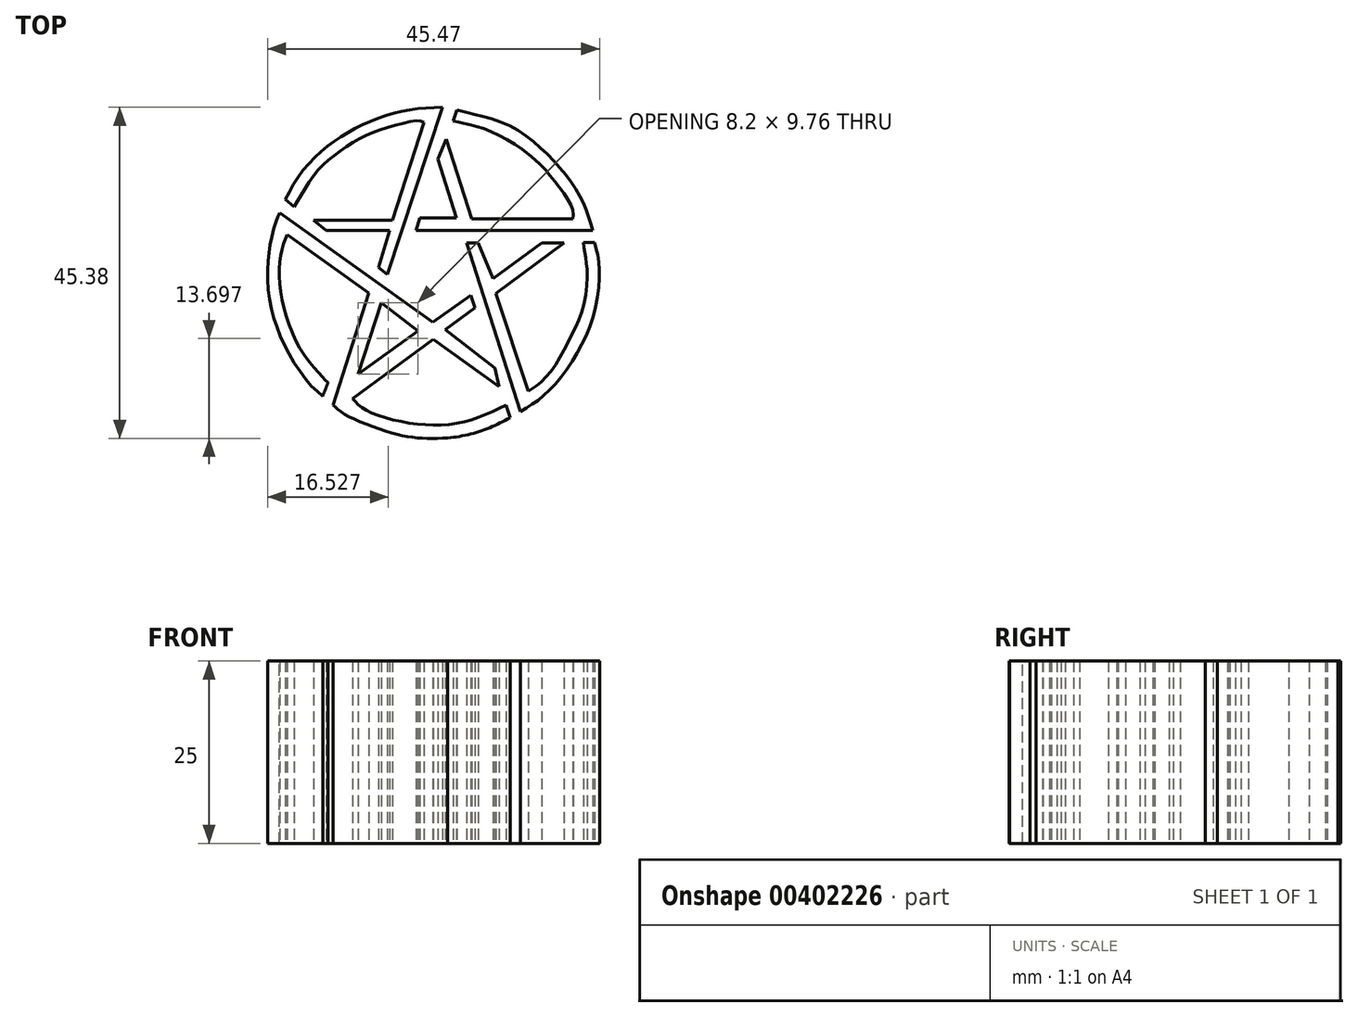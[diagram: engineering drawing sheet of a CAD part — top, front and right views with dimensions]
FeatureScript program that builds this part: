
annotation { "Feature Type Name" : "Feature", "Feature Type Description" : "" }
export const myFeature = defineFeature(function(context is Context, id is Id, definition is map)
    precondition{}
    {
        {
            var Q0;
            Q0=qCreatedBy(makeId("Top.planeOp"),FACE);
            var sketch = newSketch(context, id + "F0", { "sketchPlane" : qUnion([Q0])});
            skLineSegment(sketch, "E0", {"start": v(34.04, 53.7) * mm, "end": v(44.81, 53.7) * mm});
            skLineSegment(sketch, "E1", {"start": v(44.81, 53.7) * mm, "end": v(49.17, 67.07) * mm});
            skLineSegment(sketch, "E2", {"start": v(34.04, 53.7) * mm, "end": v(35.73, 52.33) * mm});
            skLineSegment(sketch, "E3", {"start": v(35.73, 52.33) * mm, "end": v(44.46, 52.33) * mm});
            skLineSegment(sketch, "E4", {"start": v(44.46, 52.33) * mm, "end": v(42.94, 47.22) * mm});
            skLineSegment(sketch, "E5", {"start": v(42.94, 47.22) * mm, "end": v(44.11, 46.28) * mm});
            skLineSegment(sketch, "E6", {"start": v(44.11, 46.28) * mm, "end": v(51.7, 69.18) * mm});
            skFitSpline(sketch, "E7", {"points": [v(51.7, 69.18) * mm, v(48, 68.94) * mm, v(44.54, 68.25) * mm, v(40.97, 66.87) * mm, v(37.72, 65.1) * mm, v(34.85, 62.93) * mm, v(32.08, 59.86) * mm, v(30.19, 56.57) * mm], "startDerivative": vector(-26.32, -1.03) * mm, "endDerivative": vector(-11.91, -23.24) * mm});
            skFitSpline(sketch, "E8", {"points": [v(30.19, 56.57) * mm, v(31.36, 55.54) * mm], "startDerivative": vector(1.17, -1.02) * mm, "endDerivative": vector(1.17, -1.02) * mm});
            skFitSpline(sketch, "E9", {"points": [v(31.36, 55.54) * mm, v(32.78, 57.87) * mm, v(34.73, 60.66) * mm, v(36.8, 62.53) * mm, v(39.62, 64.45) * mm, v(42.3, 65.8) * mm, v(45.8, 66.87) * mm, v(48.25, 67.35) * mm, v(49.17, 67.07) * mm], "startDerivative": vector(10.85, 17.86) * mm, "endDerivative": vector(11, -5.12) * mm});
            skLineSegment(sketch, "E10", {"start": v(69.52, 53.9) * mm, "end": v(55.7, 53.9) * mm});
            skLineSegment(sketch, "E11", {"start": v(55.7, 53.9) * mm, "end": v(52.17, 64.82) * mm});
            skLineSegment(sketch, "E12", {"start": v(52.17, 64.82) * mm, "end": v(51.04, 62.06) * mm});
            skLineSegment(sketch, "E13", {"start": v(51.04, 62.06) * mm, "end": v(53.6, 54) * mm});
            skLineSegment(sketch, "E14", {"start": v(53.6, 54) * mm, "end": v(48.57, 54) * mm});
            skLineSegment(sketch, "E15", {"start": v(48.57, 54) * mm, "end": v(48.06, 52.28) * mm});
            skLineSegment(sketch, "E16", {"start": v(48.06, 52.28) * mm, "end": v(72.28, 52.28) * mm});
            skFitSpline(sketch, "E17", {"points": [v(72.28, 52.28) * mm, v(71.22, 55.45) * mm, v(69.13, 59.2) * mm, v(65.58, 63.18) * mm, v(61, 66.58) * mm, v(55.94, 68.25) * mm, v(53.67, 68.8) * mm], "startDerivative": vector(-6.17, 21.35) * mm, "endDerivative": vector(-17.8, 3.56) * mm});
            skFitSpline(sketch, "E18", {"points": [v(53.67, 68.8) * mm, v(53.14, 67.3) * mm], "startDerivative": vector(-0.53, -1.48) * mm, "endDerivative": vector(-0.53, -1.48) * mm});
            skFitSpline(sketch, "E19", {"points": [v(53.14, 67.3) * mm, v(55.25, 66.85) * mm, v(58.75, 65.68) * mm, v(63.16, 63) * mm, v(65.95, 60.4) * mm, v(68.2, 57.5) * mm, v(69.52, 55.1) * mm, v(69.52, 53.9) * mm], "startDerivative": vector(16.75, -3.37) * mm, "endDerivative": vector(-1.88, -12.56) * mm});
            skLineSegment(sketch, "E20", {"start": v(63.45, 30.3) * mm, "end": v(59, 43.68) * mm});
            skLineSegment(sketch, "E21", {"start": v(59, 43.68) * mm, "end": v(68.32, 50.57) * mm});
            skLineSegment(sketch, "E22", {"start": v(68.32, 50.57) * mm, "end": v(65.26, 50.57) * mm});
            skLineSegment(sketch, "E23", {"start": v(65.26, 50.57) * mm, "end": v(58.59, 45.67) * mm});
            skLineSegment(sketch, "E24", {"start": v(58.59, 45.67) * mm, "end": v(56.6, 50.57) * mm});
            skLineSegment(sketch, "E25", {"start": v(56.6, 50.57) * mm, "end": v(54.97, 50.57) * mm});
            skLineSegment(sketch, "E26", {"start": v(54.97, 50.57) * mm, "end": v(62.37, 27.48) * mm});
            skFitSpline(sketch, "E27", {"points": [v(62.37, 27.48) * mm, v(65.44, 29.58) * mm, v(69.22, 34.03) * mm, v(72.32, 40.57) * mm, v(73.16, 47.2) * mm, v(72.49, 50.64) * mm], "startDerivative": vector(18.2, 10.77) * mm, "endDerivative": vector(-5.41, 19.2) * mm});
            skFitSpline(sketch, "E28", {"points": [v(72.49, 50.64) * mm, v(70.97, 50.64) * mm], "startDerivative": vector(-1.52, 0) * mm, "endDerivative": vector(-1.52, 0) * mm});
            skFitSpline(sketch, "E29", {"points": [v(70.97, 50.64) * mm, v(71.23, 48.9) * mm, v(71.48, 46.77) * mm, v(70.97, 41.87) * mm, v(69.3, 37.88) * mm, v(67.04, 33.71) * mm, v(64.86, 31.24) * mm, v(63.45, 30.3) * mm], "startDerivative": vector(2.34, -16.4) * mm, "endDerivative": vector(-12.91, -7.73) * mm});
            skLineSegment(sketch, "E30", {"start": v(40.14, 32.62) * mm, "end": v(48.35, 38.51) * mm});
            skLineSegment(sketch, "E31", {"start": v(48.35, 38.51) * mm, "end": v(43.3, 42.38) * mm});
            skLineSegment(sketch, "E32", {"start": v(43.3, 42.38) * mm, "end": v(40.14, 32.62) * mm});
            skLineSegment(sketch, "E33", {"start": v(29.4, 54.73) * mm, "end": v(50.33, 39.74) * mm});
            skLineSegment(sketch, "E34", {"start": v(50.33, 39.74) * mm, "end": v(55.55, 43.44) * mm});
            skLineSegment(sketch, "E35", {"start": v(55.55, 43.44) * mm, "end": v(56.12, 41.68) * mm});
            skLineSegment(sketch, "E36", {"start": v(56.12, 41.68) * mm, "end": v(52.06, 38.71) * mm});
            skLineSegment(sketch, "E37", {"start": v(52.06, 38.71) * mm, "end": v(58.87, 33.42) * mm});
            skLineSegment(sketch, "E38", {"start": v(58.87, 33.42) * mm, "end": v(59.43, 30.91) * mm});
            skLineSegment(sketch, "E39", {"start": v(59.43, 30.91) * mm, "end": v(50.44, 37.37) * mm});
            skLineSegment(sketch, "E40", {"start": v(50.44, 37.37) * mm, "end": v(39.34, 29.27) * mm});
            skFitSpline(sketch, "E41", {"points": [v(39.34, 29.27) * mm, v(41.09, 27.76) * mm, v(47.13, 25.91) * mm, v(54.3, 26) * mm, v(60.39, 28.35) * mm], "startDerivative": vector(8.43, -9.43) * mm, "endDerivative": vector(21.43, 10.22) * mm});
            skFitSpline(sketch, "E42", {"points": [v(60.39, 28.35) * mm, v(60.94, 26.63) * mm], "startDerivative": vector(0.55, -1.72) * mm, "endDerivative": vector(0.55, -1.72) * mm});
            skFitSpline(sketch, "E43", {"points": [v(60.94, 26.63) * mm, v(56.95, 24.82) * mm, v(52.37, 23.86) * mm], "startDerivative": vector(-7.88, -4.22) * mm, "endDerivative": vector(-9.4, -0.92) * mm});
            skFitSpline(sketch, "E44", {"points": [v(52.37, 23.86) * mm, v(48.47, 23.86) * mm, v(44.15, 24.74) * mm, v(38.4, 27.05) * mm, v(36.68, 28.39) * mm], "startDerivative": vector(-16.03, -0.6) * mm, "endDerivative": vector(-7.37, 7.1) * mm});
            skLineSegment(sketch, "E45", {"start": v(36.68, 28.39) * mm, "end": v(41.62, 43.71) * mm});
            skLineSegment(sketch, "E46", {"start": v(41.62, 43.71) * mm, "end": v(30.44, 51.73) * mm});
            skFitSpline(sketch, "E47", {"points": [v(30.44, 51.73) * mm, v(29.72, 49.75) * mm, v(29.3, 46.18) * mm, v(30.08, 41.23) * mm, v(32.36, 35.83) * mm, v(35.04, 32.45) * mm, v(36.01, 31.47) * mm], "startDerivative": vector(-5.94, -14.25) * mm, "endDerivative": vector(8.25, -7.93) * mm});
            skFitSpline(sketch, "E48", {"points": [v(36.01, 31.47) * mm, v(35.28, 29.58) * mm], "startDerivative": vector(-0.6, -1.66) * mm, "endDerivative": vector(-0.6, -1.66) * mm});
            skFitSpline(sketch, "E49", {"points": [v(35.28, 29.58) * mm, v(33.2, 31.6) * mm, v(30.56, 35.6) * mm, v(28.78, 39.69) * mm, v(27.83, 43.93) * mm, v(27.8, 48.17) * mm, v(28.27, 51.28) * mm, v(29.01, 53.86) * mm, v(29.4, 54.73) * mm], "startDerivative": vector(-17.5, 15.06) * mm, "endDerivative": vector(5.51, 11.03) * mm});
            skFitSpline(sketch, "E50", {"points": [v(48.98, 97.92) * mm, v(51.03, 96.75) * mm, v(53.35, 94.5) * mm, v(55.25, 91.65) * mm, v(55.6, 89.02) * mm, v(55.25, 86) * mm, v(54.5, 83.74) * mm, v(53.6, 81.36) * mm, v(53.16, 79.9) * mm, v(53.34, 77.77) * mm, v(53.96, 76.35) * mm, v(54.68, 75.1) * mm, v(55.25, 74.9) * mm, v(55.94, 75.48) * mm], "startDerivative": vector(24.94, -12.18) * mm, "endDerivative": vector(6.73, 19.15) * mm});
            skFitSpline(sketch, "E51", {"points": [v(55.94, 75.48) * mm, v(56.87, 76.84) * mm, v(58.58, 78.29) * mm, v(60.14, 79.6) * mm, v(61.46, 80.8) * mm, v(62.6, 82.4) * mm, v(63.4, 84.14) * mm, v(63.64, 85.48) * mm, v(63.7, 86.9) * mm, v(63.65, 87.79) * mm, v(63.57, 88.08) * mm], "startDerivative": vector(7.59, 13.14) * mm, "endDerivative": vector(-1.96, 5.62) * mm});
            skFitSpline(sketch, "E52", {"points": [v(63.57, 88.08) * mm, v(64.2, 87.56) * mm, v(64.8, 86.8) * mm, v(65.33, 85.8) * mm, v(65.89, 84.56) * mm, v(66.17, 83.5) * mm, v(66.4, 81.93) * mm, v(65.96, 80.43) * mm, v(65.24, 78.88) * mm, v(63.83, 76.9) * mm, v(62.85, 75.26) * mm, v(62.4, 74.38) * mm, v(62.3, 73.64) * mm, v(62.37, 72.64) * mm, v(62.68, 72.24) * mm], "startDerivative": vector(10.96, -8.33) * mm, "endDerivative": vector(8.06, -6.97) * mm});
            skFitSpline(sketch, "E53", {"points": [v(62.68, 72.24) * mm, v(63.23, 72.24) * mm, v(64.21, 73.18) * mm, v(65.93, 74.42) * mm, v(67.75, 75.1) * mm, v(69.88, 75.89) * mm, v(71.74, 76.8) * mm, v(73.4, 78) * mm, v(74.88, 79.81) * mm, v(75.51, 81.51) * mm, v(75.9, 82.72) * mm], "startDerivative": vector(9.62, -2.12) * mm, "endDerivative": vector(4.66, 13.44) * mm});
            skFitSpline(sketch, "E54", {"points": [v(75.9, 82.72) * mm, v(76.41, 81.51) * mm, v(76.78, 79.84) * mm, v(76.96, 78.08) * mm, v(76.85, 76.35) * mm, v(75.55, 74.85) * mm, v(73.9, 73.15) * mm, v(72.27, 71.97) * mm, v(70.64, 70.7) * mm, v(70.2, 70.03) * mm, v(70.3, 69.57) * mm, v(71.38, 69.73) * mm, v(72.94, 69.96) * mm, v(75.39, 69.98) * mm, v(77.82, 70) * mm, v(79.84, 70.56) * mm, v(82.24, 71.53) * mm, v(83.84, 73.42) * mm, v(84.53, 74.25) * mm], "startDerivative": vector(11.08, -23.6) * mm, "endDerivative": vector(14.5, 16.03) * mm});
            skFitSpline(sketch, "E55", {"points": [v(84.53, 74.25) * mm, v(85.03, 73.14) * mm, v(84.53, 70.54) * mm, v(83.39, 68.15) * mm, v(81.17, 66.47) * mm, v(78.4, 65.5) * mm, v(75.9, 64.75) * mm, v(74.54, 63.95) * mm, v(73.4, 62.36) * mm, v(72.65, 60.93) * mm, v(72.65, 60.13) * mm, v(72.98, 59.92) * mm, v(73.36, 59.84) * mm, v(74.03, 60.13) * mm, v(75.37, 61.35) * mm, v(77.8, 62.1) * mm, v(80.54, 62.31) * mm, v(82.97, 61.85) * mm, v(85.61, 61.1) * mm, v(87.92, 60.51) * mm, v(90.1, 60.22) * mm, v(92.5, 60.17) * mm, v(94.13, 60.6) * mm, v(95.52, 61.01) * mm, v(96.23, 61.56) * mm, v(97.03, 62.19) * mm, v(98.25, 63.07) * mm, v(98.7, 63.45) * mm, v(99.08, 63.49) * mm, v(99.3, 63.43) * mm, v(99.38, 62.94) * mm, v(99.17, 62.31) * mm, v(98.29, 60.68) * mm], "startDerivative": vector(23.51, -34.02) * mm, "endDerivative": vector(-27.36, -51.65) * mm});
            skFitSpline(sketch, "E56", {"points": [v(98.29, 60.68) * mm, v(97.69, 59.5) * mm, v(96.69, 57.53) * mm, v(95.5, 56.24) * mm, v(94.12, 55.33) * mm, v(91.9, 54.6) * mm, v(89.04, 54.37) * mm, v(86.47, 54.35) * mm, v(82.3, 53.66) * mm, v(80.4, 52.32) * mm, v(79.56, 51.26) * mm, v(79.7, 50.84) * mm, v(80.05, 50.77) * mm, v(81.32, 50.42) * mm, v(83.16, 49.64) * mm, v(85.41, 48.23) * mm, v(88.3, 46.82) * mm, v(90.57, 46.46) * mm, v(92.83, 46.82) * mm, v(95.01, 47.6) * mm], "startDerivative": vector(-13.33, -24.83) * mm, "endDerivative": vector(37.72, 14.89) * mm});
            skFitSpline(sketch, "E57", {"points": [v(95.01, 47.6) * mm, v(94.35, 45.8) * mm, v(92.25, 43.88) * mm, v(90.28, 42.53) * mm, v(88.16, 42.45) * mm, v(85.52, 42.93) * mm, v(83.3, 43.55) * mm, v(81.9, 43.88) * mm, v(80.68, 43.85) * mm, v(79.95, 43.48) * mm, v(79.83, 43.03) * mm, v(80.1, 42.65) * mm, v(80.72, 42.35) * mm, v(82.35, 41.03) * mm, v(83.82, 39.3) * mm, v(85.8, 36.84) * mm, v(87.86, 35.3) * mm, v(89.5, 34.5) * mm, v(90.78, 34.2) * mm, v(92.1, 34.2) * mm, v(93.2, 34) * mm, v(93.05, 33.6) * mm, v(91.5, 32.67) * mm, v(88.6, 31.45) * mm, v(85.47, 31.95) * mm, v(82.5, 33.6) * mm, v(80.35, 35.14) * mm, v(79.83, 35.4) * mm, v(79.4, 35.3) * mm, v(79.55, 34.77) * mm, v(80.13, 33.37) * mm, v(81.32, 30.25) * mm, v(82.15, 27.88) * mm, v(83.52, 25.6) * mm, v(85.9, 23.76) * mm, v(87.84, 23.29) * mm], "startDerivative": vector(-13.57, -61.65) * mm, "endDerivative": vector(62.4, -8.3) * mm});
            skFitSpline(sketch, "E58", {"points": [v(87.86, 23.31) * mm, v(87.51, 22.54) * mm, v(85.34, 22.12) * mm, v(82.25, 22.2) * mm, v(79.68, 23.91) * mm, v(78.06, 25.66) * mm, v(76.43, 28.28) * mm, v(74.51, 29.68) * mm, v(71.9, 30.15) * mm, v(70.94, 29.83) * mm, v(70.97, 29.15) * mm, v(71.84, 28.53) * mm, v(73.79, 26.88) * mm, v(74.84, 24.76) * mm, v(75.68, 22.96) * mm, v(75.76, 19.67) * mm, v(75.63, 16.93) * mm, v(76.2, 13.6) * mm, v(77.16, 11.09) * mm, v(78.43, 8.92) * mm, v(79.95, 7.5) * mm, v(81.82, 6.5) * mm, v(81.97, 6.02) * mm, v(81.62, 5.55) * mm, v(77.96, 6.07) * mm, v(75.16, 6.75) * mm, v(74.79, 6.85) * mm, v(72.64, 8.4) * mm, v(70.8, 11.51) * mm, v(69.32, 15.73) * mm, v(67.8, 18.75) * mm, v(65.83, 20.34) * mm, v(64.16, 21.1) * mm, v(63.4, 20.47) * mm, v(63.56, 19.5) * mm, v(63.7, 18.77) * mm, v(63.26, 16.78) * mm, v(62.8, 14.68) * mm], "startDerivative": vector(-9.22, -50.5) * mm, "endDerivative": vector(-11.7, -71.76) * mm});
            skFitSpline(sketch, "E59", {"points": [v(62.8, 14.68) * mm, v(62.29, 12.53) * mm, v(62.21, 9.96) * mm, v(62.8, 7.42) * mm, v(64.16, 5.87) * mm, v(64.6, 5.12) * mm], "startDerivative": vector(-2.95, -9.97) * mm, "endDerivative": vector(2.52, -5.43) * mm});
            skFitSpline(sketch, "E60", {"points": [v(64.6, 5.12) * mm, v(63.48, 5.12) * mm, v(60.31, 6.5) * mm, v(58.47, 8.9) * mm, v(57.74, 12.21) * mm, v(57.67, 15.5) * mm, v(57.34, 17.18) * mm, v(56.57, 17.8) * mm, v(55.8, 17.77) * mm, v(55.45, 16.05) * mm, v(54.33, 14.03) * mm, v(53.13, 12.14) * mm, v(51.78, 9.96) * mm, v(50.88, 7.92) * mm, v(50.7, 5.77) * mm, v(51.1, 3.98) * mm, v(51.53, 2.78) * mm, v(51.5, 2.45) * mm, v(50.58, 2.7) * mm, v(48.46, 5.12) * mm, v(47.36, 6.82) * mm, v(47.36, 9.5) * mm, v(47.94, 12.53) * mm, v(48.61, 14.68) * mm, v(48.61, 15.68) * mm, v(48.24, 15.75) * mm, v(47.74, 15.38) * mm, v(46.86, 14.4) * mm, v(44.87, 12.98) * mm, v(42.8, 11.51) * mm, v(41.42, 9.94) * mm], "startDerivative": vector(-36.79, -4.78) * mm, "endDerivative": vector(-35.36, -45.94) * mm});
            skFitSpline(sketch, "E61", {"points": [v(41.42, 9.94) * mm, v(40.5, 8.57) * mm, v(39.7, 6.62) * mm, v(39.6, 5) * mm, v(39.53, 4) * mm, v(39.33, 3.98) * mm, v(38.58, 4.9) * mm, v(36.96, 8.24) * mm, v(37.36, 11.84) * mm, v(39.18, 14.38) * mm, v(41.42, 16.93) * mm, v(41.6, 21.17) * mm, v(40.83, 22.07) * mm, v(40.43, 21.97) * mm, v(39.9, 21.24) * mm, v(39.5, 19.5) * mm, v(37.68, 17.23) * mm, v(35.34, 15.48) * mm, v(31.42, 14.26) * mm, v(28.4, 12.93) * mm, v(25.53, 11.34) * mm, v(23.63, 9.37) * mm, v(22.39, 6.72) * mm, v(21.66, 5.07) * mm, v(21.31, 4.1) * mm], "startDerivative": vector(-25.4, -34.57) * mm, "endDerivative": vector(-10.6, -31.93) * mm});
            skFitSpline(sketch, "E62", {"points": [v(21.31, 4.1) * mm, v(20.54, 6.1) * mm, v(20.14, 9.7) * mm, v(20.04, 12.93) * mm, v(22.29, 15.8) * mm, v(25.38, 18.45) * mm, v(28.52, 20.82) * mm, v(29.75, 22.92) * mm, v(30.12, 24.54) * mm, v(29.8, 24.96) * mm, v(29.25, 25.01) * mm, v(28.2, 24.39) * mm, v(25.9, 24.24) * mm, v(22.76, 24.24) * mm, v(20.79, 23.69) * mm, v(18.6, 22.52) * mm, v(16.82, 20.54) * mm, v(16.12, 19.72) * mm, v(15.8, 19.25) * mm, v(15.67, 20) * mm, v(15.77, 22.54) * mm, v(16.52, 25.66) * mm, v(19.3, 27.63) * mm, v(21.66, 28.65) * mm, v(23.46, 29.33) * mm, v(25.33, 30.45) * mm, v(25.58, 31.17) * mm, v(25.39, 31.74) * mm, v(24.34, 31.6) * mm, v(23, 31.45) * mm, v(20.08, 32.08) * mm, v(17.06, 32.9) * mm, v(14.27, 33.04) * mm, v(12.34, 32.79) * mm, v(10.4, 31.89) * mm, v(9.07, 31.07) * mm, v(9.02, 31.93) * mm, v(10.16, 34.49) * mm, v(12.15, 36.76) * mm, v(15.23, 37.57) * mm, v(17.6, 37.62) * mm, v(19.22, 37.57) * mm, v(21.03, 37.89) * mm, v(21.31, 38.29) * mm, v(20.71, 38.7) * mm, v(18.2, 39.9) * mm, v(15.61, 41.98) * mm, v(13.5, 43.24) * mm, v(10.66, 43.74) * mm, v(7.43, 43.26) * mm, v(6.55, 42.9) * mm, v(6.42, 43.2) * mm, v(6.95, 43.83) * mm, v(9.2, 46.05) * mm, v(11.1, 47.27) * mm, v(12.88, 47.37) * mm, v(15.6, 47.04) * mm, v(18.21, 46.1) * mm, v(20.42, 45.46) * mm, v(22.37, 45.88) * mm, v(23.86, 46.79) * mm, v(24.13, 47.29) * mm, v(23.63, 47.56) * mm, v(20.98, 47.65) * mm, v(17.77, 48.97) * mm, v(14.94, 51.55) * mm, v(12.44, 54.99) * mm, v(10.37, 57.02) * mm, v(7.51, 58.96) * mm, v(5.2, 59.73) * mm, v(2.67, 59.9) * mm, v(1.03, 59.82) * mm, v(1.22, 60.26) * mm, v(2.27, 61.01) * mm, v(5.18, 62.71) * mm, v(8.37, 63.74) * mm, v(11.04, 63.24) * mm, v(13.64, 62.08) * mm, v(17.6, 59.08) * mm, v(19.58, 57.97) * mm, v(22.16, 57.76) * mm, v(24.86, 58.16) * mm, v(25.62, 59) * mm, v(24.03, 60.74) * mm, v(22.4, 64.39) * mm, v(21.31, 66.76) * mm, v(18.97, 69.47) * mm, v(15.86, 70.85) * mm, v(14.29, 71.3) * mm, v(15.82, 72.13) * mm, v(19.51, 72.5) * mm, v(21.31, 72.4) * mm, v(23.85, 70.73) * mm, v(25.86, 68.19) * mm, v(27.49, 66.56) * mm, v(28.97, 65.61) * mm, v(29.96, 65.61) * mm, v(29.53, 66.6) * mm, v(28.55, 68.72) * mm, v(28.55, 71.15) * mm, v(28.37, 74.79) * mm], "startDerivative": vector(-90.17, 182.19) * mm, "endDerivative": vector(-24.72, 293.76) * mm});
            skFitSpline(sketch, "E63", {"points": [v(28.37, 74.79) * mm, v(27.8, 76.94) * mm, v(26.53, 78.99) * mm, v(24.52, 80.9) * mm, v(23.85, 81.5) * mm, v(24.52, 81.84) * mm, v(26.53, 81.6) * mm, v(29.53, 80.82) * mm, v(30.9, 79.62) * mm, v(32.36, 77.15) * mm, v(33.17, 74.79) * mm, v(34.09, 72.25) * mm, v(34.58, 72) * mm, v(34.8, 72.21) * mm, v(35.25, 75.35) * mm, v(36.63, 79.02) * mm, v(36.94, 81.31) * mm, v(36.3, 84.38) * mm, v(34.58, 87.2) * mm, v(35.74, 87) * mm, v(38.46, 85.51) * mm, v(40.58, 83.5) * mm, v(41, 80.15) * mm, v(41.07, 75.17) * mm, v(41.42, 73.66) * mm, v(43.5, 71.72) * mm, v(44.46, 71.65) * mm, v(44.35, 73.02) * mm, v(43.58, 75.17) * mm, v(44.18, 79.02) * mm, v(44.64, 79.62) * mm, v(45.8, 82.76) * mm, v(48.98, 86.96) * mm, v(50.39, 91.8) * mm, v(49.68, 95.43) * mm, v(48.98, 97.92) * mm], "startDerivative": vector(-15.85, 79.8) * mm, "endDerivative": vector(-22.22, 80.45) * mm});
            skSolve(sketch);
        }
        {
            var Q0;
            Q0 = qSketchRegion(id + "F0", true);
            extrude(context, id + "F1", {"entities" : qUnion([Q0]), "depth" : 25 * mm, "offsetDistance" : 25 * mm});
        }
    });
